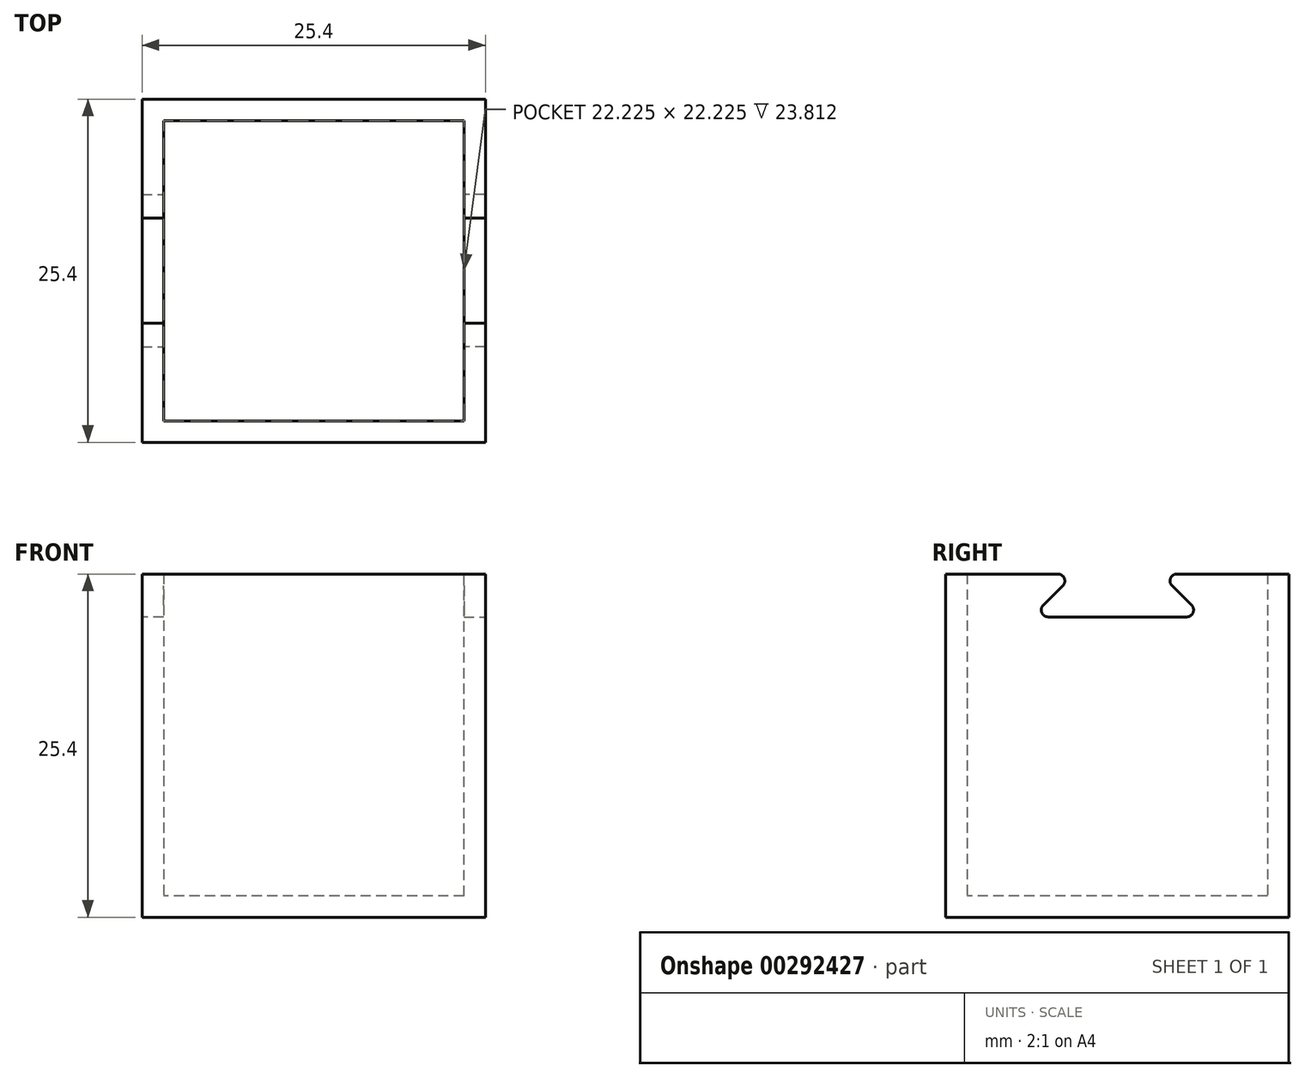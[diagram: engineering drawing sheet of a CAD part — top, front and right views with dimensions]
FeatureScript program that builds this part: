
annotation { "Feature Type Name" : "Feature", "Feature Type Description" : "" }
export const myFeature = defineFeature(function(context is Context, id is Id, definition is map)
    precondition{}
    {
        {
            var Q0;
            Q0=qCreatedBy(makeId("Top.planeOp"),FACE);
            var sketch = newSketch(context, id + "F0", { "sketchPlane" : qUnion([Q0])});
            skLineSegment(sketch, "E0.bottom", {"start": v(-7.17, 5.15) * mm, "end": v(18.23, 5.15) * mm});
            skLineSegment(sketch, "E0.top", {"start": v(-7.17, -20.25) * mm, "end": v(18.23, -20.25) * mm});
            skLineSegment(sketch, "E0.left", {"start": v(-7.17, 5.15) * mm, "end": v(-7.17, -20.25) * mm});
            skLineSegment(sketch, "E0.right", {"start": v(18.23, 5.15) * mm, "end": v(18.23, -20.25) * mm});
            skSolve(sketch);
        }
        {
            var Q0;
            Q0 = qSketchRegion(id + "F0", true);
            extrude(context, id + "F1", {"entities" : qUnion([Q0]), "depth" : 1.59 * mm});
        }
        {
            var Q0;
            Q0=makeQuery(id+"F1.opExtrude","SWEPT_FACE",FACE,{"disambiguationData":[OSD([sQuery(id+"F0.wireOp",EDGE,"E0.top")])]});
            var sketch = newSketch(context, id + "F2", { "sketchPlane" : qUnion([Q0])});
            skLineSegment(sketch, "E1.bottom", {"start": v(-7.17, 0) * mm, "end": v(18.23, 0) * mm});
            skLineSegment(sketch, "E1.top", {"start": v(-7.17, 25.4) * mm, "end": v(18.23, 25.4) * mm});
            skLineSegment(sketch, "E1.left", {"start": v(-7.17, 0) * mm, "end": v(-7.17, 25.4) * mm});
            skLineSegment(sketch, "E1.right", {"start": v(18.23, 0) * mm, "end": v(18.23, 25.4) * mm});
            skSolve(sketch);
        }
        {
            var Q0;
            Q0 = qSketchRegion(id + "F2", true);
            extrude(context, id + "F3", {"entities" : qUnion([Q0]), "operationType" : NewBodyOperationType.ADD, "oppositeDirection" : true, "depth" : 1.59 * mm});
        }
        {
            var Q0;
            Q0=makeQuery(id+"F1.opExtrude","SWEPT_FACE",FACE,{"disambiguationData":[OSD([sQuery(id+"F0.wireOp",EDGE,"E0.bottom")])]});
            var sketch = newSketch(context, id + "F4", { "sketchPlane" : qUnion([Q0])});
            skLineSegment(sketch, "E2.bottom", {"start": v(-18.23, 0) * mm, "end": v(7.17, 0) * mm});
            skLineSegment(sketch, "E2.top", {"start": v(-18.23, 25.4) * mm, "end": v(7.17, 25.4) * mm});
            skLineSegment(sketch, "E2.left", {"start": v(-18.23, 0) * mm, "end": v(-18.23, 25.4) * mm});
            skLineSegment(sketch, "E2.right", {"start": v(7.17, 0) * mm, "end": v(7.17, 25.4) * mm});
            skSolve(sketch);
        }
        {
            var Q0;
            Q0 = qSketchRegion(id + "F4", true);
            extrude(context, id + "F5", {"entities" : qUnion([Q0]), "operationType" : NewBodyOperationType.ADD, "oppositeDirection" : true, "depth" : 1.59 * mm});
        }
        {
            var Q0;
            Q0=makeQuery(id+"F5.boolean.opBoolean","MERGE",FACE,{"derivedFrom":[makeQuery(id+"F3.boolean.opBoolean","MERGE",FACE,{"derivedFrom":[makeQuery(id+"F1.opExtrude","SWEPT_FACE",FACE,{"disambiguationData":[OSD([sQuery(id+"F0.wireOp",EDGE,"E0.right")])]}),makeQuery(id+"F3.opExtrude","SWEPT_FACE",FACE,{"disambiguationData":[OSD([sQuery(id+"F2.wireOp",EDGE,"E1.right")])]})]}),makeQuery(id+"F5.opExtrude","SWEPT_FACE",FACE,{"disambiguationData":[OSD([sQuery(id+"F4.wireOp",EDGE,"E2.left")])]})]});
            var sketch = newSketch(context, id + "F6", { "sketchPlane" : qUnion([Q0])});
            skLineSegment(sketch, "E3.bottom", {"start": v(-20.25, 0) * mm, "end": v(5.15, 0) * mm});
            skLineSegment(sketch, "E3.top", {"start": v(-20.25, 25.4) * mm, "end": v(-10.73, 25.4) * mm});
            skLineSegment(sketch, "E3.left", {"start": v(-20.25, 0) * mm, "end": v(-20.25, 25.4) * mm});
            skLineSegment(sketch, "E3.right", {"start": v(5.15, 0) * mm, "end": v(5.15, 25.4) * mm});
            skLineSegment(sketch, "E4", {"start": v(-10.73, 25.4) * mm, "end": v(-13.9, 22.23) * mm});
            skLineSegment(sketch, "E5", {"start": v(-13.9, 22.23) * mm, "end": v(-1.2, 22.23) * mm});
            skLineSegment(sketch, "E6", {"start": v(-1.2, 22.23) * mm, "end": v(-4.38, 25.4) * mm});
            skLineSegment(sketch, "E7.trimOffspring", {"start": v(-4.38, 25.4) * mm, "end": v(5.15, 25.4) * mm});
            skSolve(sketch);
        }
        {
            var Q0;
            Q0 = qSketchRegion(id + "F6", true);
            extrude(context, id + "F7", {"entities" : qUnion([Q0]), "operationType" : NewBodyOperationType.ADD, "oppositeDirection" : true, "depth" : 1.59 * mm});
        }
        {
            var Q0;
            Q0=makeQuery(id+"F5.boolean.opBoolean","MERGE",FACE,{"derivedFrom":[makeQuery(id+"F3.boolean.opBoolean","MERGE",FACE,{"derivedFrom":[makeQuery(id+"F1.opExtrude","SWEPT_FACE",FACE,{"disambiguationData":[OSD([sQuery(id+"F0.wireOp",EDGE,"E0.left")])]}),makeQuery(id+"F3.opExtrude","SWEPT_FACE",FACE,{"disambiguationData":[OSD([sQuery(id+"F2.wireOp",EDGE,"E1.left")])]})]}),makeQuery(id+"F5.opExtrude","SWEPT_FACE",FACE,{"disambiguationData":[OSD([sQuery(id+"F4.wireOp",EDGE,"E2.right")])]})]});
            var sketch = newSketch(context, id + "F8", { "sketchPlane" : qUnion([Q0])});
            skLineSegment(sketch, "E8.bottom", {"start": v(-5.15, 25.4) * mm, "end": v(4.38, 25.4) * mm});
            skLineSegment(sketch, "E8.top", {"start": v(-5.15, 0) * mm, "end": v(20.25, 0) * mm});
            skLineSegment(sketch, "E8.left", {"start": v(-5.15, 25.4) * mm, "end": v(-5.15, 0) * mm});
            skLineSegment(sketch, "E8.right", {"start": v(20.25, 25.4) * mm, "end": v(20.25, 0) * mm});
            skLineSegment(sketch, "E9", {"start": v(4.38, 25.4) * mm, "end": v(1.2, 22.23) * mm});
            skLineSegment(sketch, "E10", {"start": v(1.2, 22.23) * mm, "end": v(13.9, 22.23) * mm});
            skLineSegment(sketch, "E11", {"start": v(13.9, 22.23) * mm, "end": v(10.73, 25.4) * mm});
            skLineSegment(sketch, "E12.trimOffspring", {"start": v(10.73, 25.4) * mm, "end": v(20.25, 25.4) * mm});
            skSolve(sketch);
        }
        {
            var Q0;
            Q0 = qSketchRegion(id + "F6", true);
            extrude(context, id + "F9", {"entities" : qUnion([Q0]), "operationType" : NewBodyOperationType.ADD, "oppositeDirection" : true, "depth" : 1.59 * mm});
        }
        {
            var Q0;
            {var subQ1=sQuery(id+"F8.wireOp",EDGE,"E9");Q0=makeQuery(id+"F8.imprint","IMPRINT",FACE,{"disambiguationData":[TD([[makeQuery(id+"F8.imprint","IMPRINT",EDGE,{"derivedFrom":subQ1}),-1.0]])]});}
            extrude(context, id + "F10", {"entities" : qUnion([Q0]), "operationType" : NewBodyOperationType.ADD, "oppositeDirection" : true, "depth" : 1.59 * mm});
        }
        {
            var Q0;
            Q0=makeQuery(id+"F10.opExtrude","SWEPT_EDGE",EDGE,{"disambiguationData":[OSD([sQuery(id+"F8.wireOp",EDGE,"E9"),sQuery(id+"F8.wireOp",EDGE,"E10")])]});
            fillet(context, id + "F11", {"entities" : qUnion([Q0]), "radius" : 0.5 * mm, "tangentPropagation" : true, "allowEdgeOverflow" : false});
        }
        {
            var Q0;
            Q0=makeQuery(id+"F10.opExtrude","SWEPT_EDGE",EDGE,{"disambiguationData":[OSD([sQuery(id+"F8.wireOp",EDGE,"E10"),sQuery(id+"F8.wireOp",EDGE,"E11")])]});
            fillet(context, id + "F12", {"entities" : qUnion([Q0]), "radius" : 0.5 * mm, "tangentPropagation" : true, "allowEdgeOverflow" : false});
        }
        {
            var Q0;
            Q0=makeQuery(id+"F7.opExtrude","SWEPT_EDGE",EDGE,{"disambiguationData":[OSD([sQuery(id+"F6.wireOp",EDGE,"E4"),sQuery(id+"F6.wireOp",EDGE,"E5")])]});
            fillet(context, id + "F13", {"entities" : qUnion([Q0]), "radius" : 0.5 * mm, "tangentPropagation" : true, "allowEdgeOverflow" : false});
        }
        {
            var Q0;
            Q0=makeQuery(id+"F7.opExtrude","SWEPT_EDGE",EDGE,{"disambiguationData":[OSD([sQuery(id+"F6.wireOp",EDGE,"E5"),sQuery(id+"F6.wireOp",EDGE,"E6")])]});
            fillet(context, id + "F14", {"entities" : qUnion([Q0]), "radius" : 0.5 * mm, "tangentPropagation" : true, "allowEdgeOverflow" : false});
        }
        {
            var Q0;
            Q0=makeQuery(id+"F7.opExtrude","SWEPT_EDGE",EDGE,{"disambiguationData":[OSD([sQuery(id+"F6.wireOp",EDGE,"E6"),sQuery(id+"F6.wireOp",EDGE,"E7.trimOffspring")])]});
            fillet(context, id + "F15", {"entities" : qUnion([Q0]), "radius" : 0.5 * mm, "tangentPropagation" : true, "allowEdgeOverflow" : false});
        }
        {
            var Q0;
            Q0=makeQuery(id+"F7.opExtrude","SWEPT_EDGE",EDGE,{"disambiguationData":[OSD([sQuery(id+"F6.wireOp",EDGE,"E3.top"),sQuery(id+"F6.wireOp",EDGE,"E4")])]});
            fillet(context, id + "F16", {"entities" : qUnion([Q0]), "radius" : 0.5 * mm, "tangentPropagation" : true, "allowEdgeOverflow" : false});
        }
        {
            var Q0;
            Q0=makeQuery(id+"F10.opExtrude","SWEPT_EDGE",EDGE,{"disambiguationData":[OSD([sQuery(id+"F8.wireOp",EDGE,"E8.bottom"),sQuery(id+"F8.wireOp",EDGE,"E9")])]});
            var Q1;
            Q1=makeQuery(id+"F10.opExtrude","SWEPT_EDGE",EDGE,{"disambiguationData":[OSD([sQuery(id+"F8.wireOp",EDGE,"E11"),sQuery(id+"F8.wireOp",EDGE,"E12.trimOffspring")])]});
            fillet(context, id + "F17", {"entities" : qUnion([Q0, Q1]), "radius" : 0.5 * mm, "tangentPropagation" : true, "allowEdgeOverflow" : false});
        }
    });
